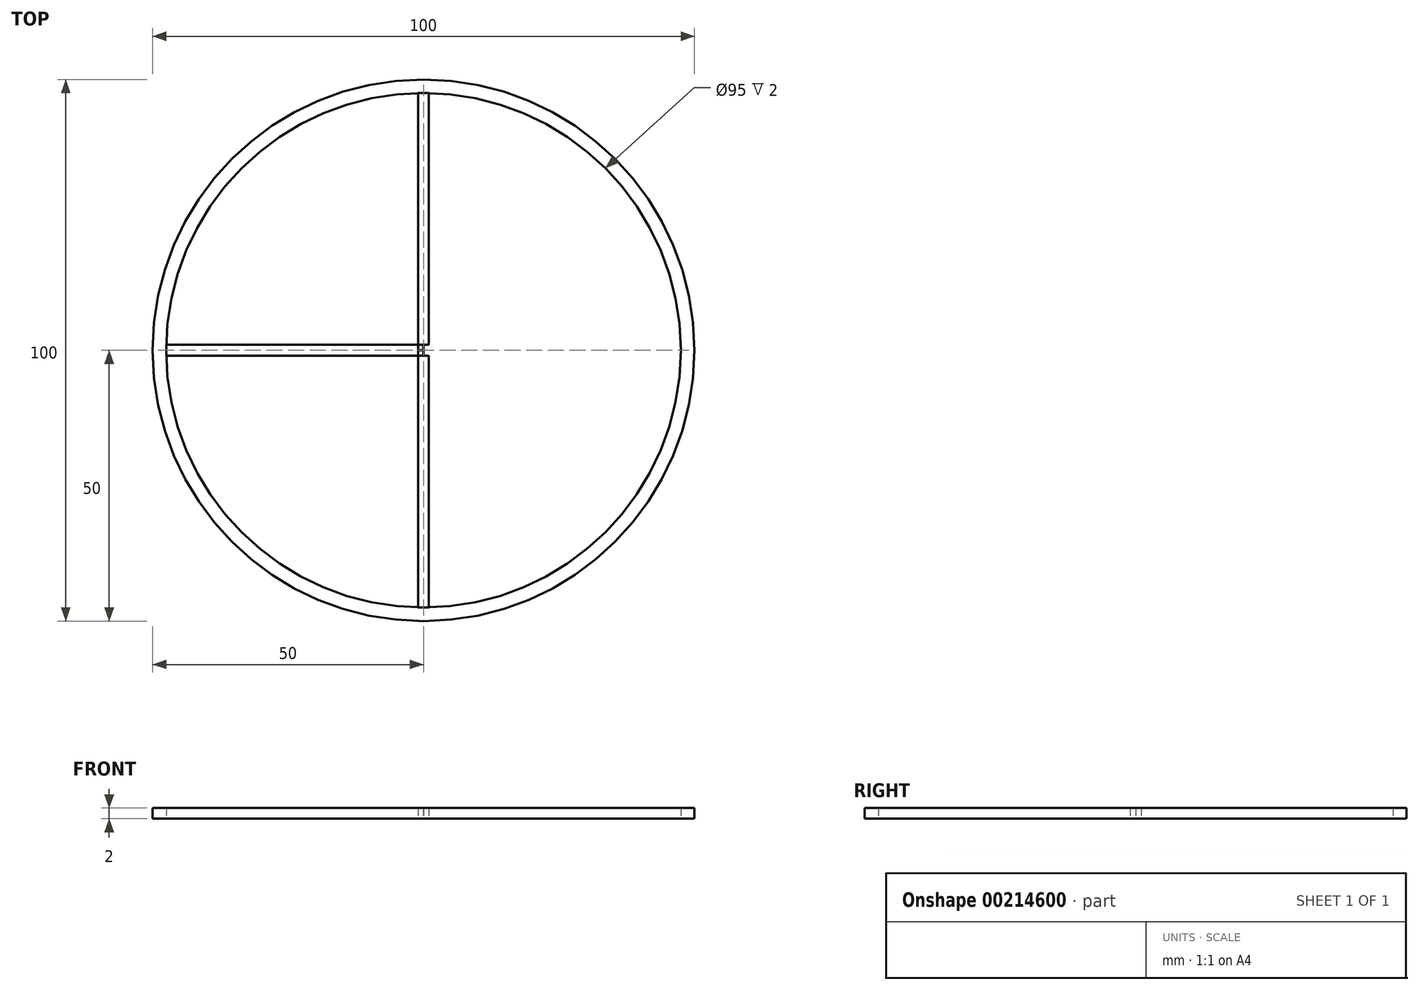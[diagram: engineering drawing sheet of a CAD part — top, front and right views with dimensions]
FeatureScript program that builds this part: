
annotation { "Feature Type Name" : "Feature", "Feature Type Description" : "" }
export const myFeature = defineFeature(function(context is Context, id is Id, definition is map)
    precondition{}
    {
        {
            var Q0;
            Q0=qCreatedBy(makeId("Top.planeOp"),FACE);
            var sketch = newSketch(context, id + "F0", { "sketchPlane" : qUnion([Q0])});
            skCircle(sketch, "E0", {"center": v(0, 0) * mm, "radius": 50 * mm});
            skCircle(sketch, "E1", {"center": v(0, 0) * mm, "radius": 47.5 * mm});
            skLineSegment(sketch, "E2", {"start": v(0, 0) * mm, "end": v(0, 47.5) * mm});
            skLineSegment(sketch, "E3", {"start": v(0, 0) * mm, "end": v(47.5, 0) * mm});
            skLineSegment(sketch, "E4", {"start": v(47.5, 0) * mm, "end": v(0, 0) * mm});
            skLineSegment(sketch, "E5", {"start": v(0, 0) * mm, "end": v(-47.5, 0) * mm});
            skLineSegment(sketch, "E6", {"start": v(0, 0) * mm, "end": v(0, -47.5) * mm});
            skLineSegment(sketch, "E7.bottom", {"start": v(1, 47.49) * mm, "end": v(-1, 47.49) * mm});
            skLineSegment(sketch, "E7.top", {"start": v(1, 0.01) * mm, "end": v(-1, 0.01) * mm});
            skLineSegment(sketch, "E7.left", {"start": v(1, 47.49) * mm, "end": v(1, 0.01) * mm});
            skLineSegment(sketch, "E7.right", {"start": v(-1, 47.49) * mm, "end": v(-1, 0.01) * mm});
            skPoint(sketch, "E7.middle", {"position": v(0, 23.75) * mm});
            skLineSegment(sketch, "E8.bottom", {"start": v(-47.49, 1) * mm, "end": v(-0.01, 1) * mm});
            skLineSegment(sketch, "E8.top", {"start": v(-47.49, -1) * mm, "end": v(-0.01, -1) * mm});
            skLineSegment(sketch, "E8.left", {"start": v(-47.49, 1) * mm, "end": v(-47.49, -1) * mm});
            skLineSegment(sketch, "E8.right", {"start": v(-0.01, 1) * mm, "end": v(-0.01, -1) * mm});
            skPoint(sketch, "E8.middle", {"position": v(-23.75, 0) * mm});
            skLineSegment(sketch, "E9.bottom", {"start": v(1, -47.49) * mm, "end": v(-1, -47.49) * mm});
            skLineSegment(sketch, "E9.top", {"start": v(1, -0.01) * mm, "end": v(-1, -0.01) * mm});
            skLineSegment(sketch, "E9.left", {"start": v(1, -47.49) * mm, "end": v(1, -0.01) * mm});
            skLineSegment(sketch, "E9.right", {"start": v(-1, -47.49) * mm, "end": v(-1, -0.01) * mm});
            skPoint(sketch, "E9.middle", {"position": v(0, -23.75) * mm});
            skLineSegment(sketch, "E10.bottom", {"start": v(47.49, 1) * mm, "end": v(0.01, 1) * mm});
            skLineSegment(sketch, "E10.top", {"start": v(47.49, -1) * mm, "end": v(0.01, -1) * mm});
            skLineSegment(sketch, "E10.left", {"start": v(47.49, 1) * mm, "end": v(47.49, -1) * mm});
            skLineSegment(sketch, "E10.right", {"start": v(0.01, 1) * mm, "end": v(0.01, -1) * mm});
            skPoint(sketch, "E10.middle", {"position": v(23.75, 0) * mm});
            skSolve(sketch);
        }
        {
            var Q0;
            Q0=makeQuery(id+"F0.imprint","IMPRINT",FACE,{"disambiguationData":[TD([[makeQuery(id+"F0.imprint","IMPRINT",EDGE,{"derivedFrom":sQuery(id+"F0.wireOp",EDGE,"E0")}),1.0]])]});
            var Q1;
            {var subQ0=sQuery(id+"F0.wireOp",EDGE,"E8.right");var subQ1=sQuery(id+"F0.wireOp",EDGE,"E5");var subQ2=makeQuery(id+"F0.imprint","INTERSECT",VERTEX,{"derivedFrom":[subQ1,subQ0]});Q1=makeQuery(id+"F0.imprint","IMPRINT",FACE,{"disambiguationData":[TD([[makeQuery(id+"F0.imprint","IMPRINT",EDGE,{"disambiguationData":[TD([[subQ2,-1.0]])],"derivedFrom":subQ1}),1.0]])]});}
            var Q2;
            {var subQ3=sQuery(id+"F0.wireOp",EDGE,"E8.right");var subQ9=sQuery(id+"F0.wireOp",EDGE,"E5");var subQ10=makeQuery(id+"F0.imprint","INTERSECT",VERTEX,{"derivedFrom":[subQ9,subQ3]});Q2=makeQuery(id+"F0.imprint","IMPRINT",FACE,{"disambiguationData":[TD([[makeQuery(id+"F0.imprint","IMPRINT",EDGE,{"disambiguationData":[TD([[subQ10,-1.0]])],"derivedFrom":subQ9}),-1.0]])]});}
            var Q3;
            {var subQ5=sQuery(id+"F0.wireOp",EDGE,"E7.top");var subQ6=sQuery(id+"F0.wireOp",EDGE,"E2");var subQ7=makeQuery(id+"F0.imprint","INTERSECT",VERTEX,{"derivedFrom":[subQ6,subQ5]});Q3=makeQuery(id+"F0.imprint","IMPRINT",FACE,{"disambiguationData":[TD([[makeQuery(id+"F0.imprint","IMPRINT",EDGE,{"disambiguationData":[TD([[subQ7,-1.0]])],"derivedFrom":subQ6}),1.0]])]});}
            var Q4;
            {var subQ5=sQuery(id+"F0.wireOp",EDGE,"E2");var subQ7=sQuery(id+"F0.wireOp",EDGE,"E7.top");var subQ8=makeQuery(id+"F0.imprint","INTERSECT",VERTEX,{"derivedFrom":[subQ5,subQ7]});Q4=makeQuery(id+"F0.imprint","IMPRINT",FACE,{"disambiguationData":[TD([[makeQuery(id+"F0.imprint","IMPRINT",EDGE,{"disambiguationData":[TD([[subQ8,-1.0]])],"derivedFrom":subQ5}),-1.0]])]});}
            var Q5;
            {var subQ5=sQuery(id+"F0.wireOp",EDGE,"E10.left");var subQ9=sQuery(id+"F0.wireOp",EDGE,"E4");var subQ10=makeQuery(id+"F0.imprint","INTERSECT",VERTEX,{"derivedFrom":[subQ9,subQ5]});Q5=makeQuery(id+"F0.imprint","IMPRINT",FACE,{"disambiguationData":[TD([[makeQuery(id+"F0.imprint","IMPRINT",EDGE,{"disambiguationData":[TD([[subQ10,-1.0]])],"derivedFrom":subQ9}),-1.0]])]});}
            var Q6;
            {var subQ0=sQuery(id+"F0.wireOp",EDGE,"E10.left");var subQ9=sQuery(id+"F0.wireOp",EDGE,"E4");var subQ10=makeQuery(id+"F0.imprint","INTERSECT",VERTEX,{"derivedFrom":[subQ9,subQ0]});Q6=makeQuery(id+"F0.imprint","IMPRINT",FACE,{"disambiguationData":[TD([[makeQuery(id+"F0.imprint","IMPRINT",EDGE,{"disambiguationData":[TD([[subQ10,-1.0]])],"derivedFrom":subQ9}),1.0]])]});}
            var Q7;
            {var subQ7=sQuery(id+"F0.wireOp",EDGE,"E6");var subQ9=sQuery(id+"F0.wireOp",EDGE,"E9.top");var subQ10=makeQuery(id+"F0.imprint","INTERSECT",VERTEX,{"derivedFrom":[subQ7,subQ9]});Q7=makeQuery(id+"F0.imprint","IMPRINT",FACE,{"disambiguationData":[TD([[makeQuery(id+"F0.imprint","IMPRINT",EDGE,{"disambiguationData":[TD([[subQ10,-1.0]])],"derivedFrom":subQ7}),1.0]])]});}
            var Q8;
            {var subQ3=sQuery(id+"F0.wireOp",EDGE,"E6");var subQ9=sQuery(id+"F0.wireOp",EDGE,"E9.top");var subQ11=makeQuery(id+"F0.imprint","INTERSECT",VERTEX,{"derivedFrom":[subQ3,subQ9]});Q8=makeQuery(id+"F0.imprint","IMPRINT",FACE,{"disambiguationData":[TD([[makeQuery(id+"F0.imprint","IMPRINT",EDGE,{"disambiguationData":[TD([[subQ11,-1.0]])],"derivedFrom":subQ3}),-1.0]])]});}
            extrude(context, id + "F1", {"entities" : qUnion([Q0, Q1, Q2, Q3, Q4, Q5, Q6, Q7, Q8]), "depth" : 2 * mm});
        }
    });
